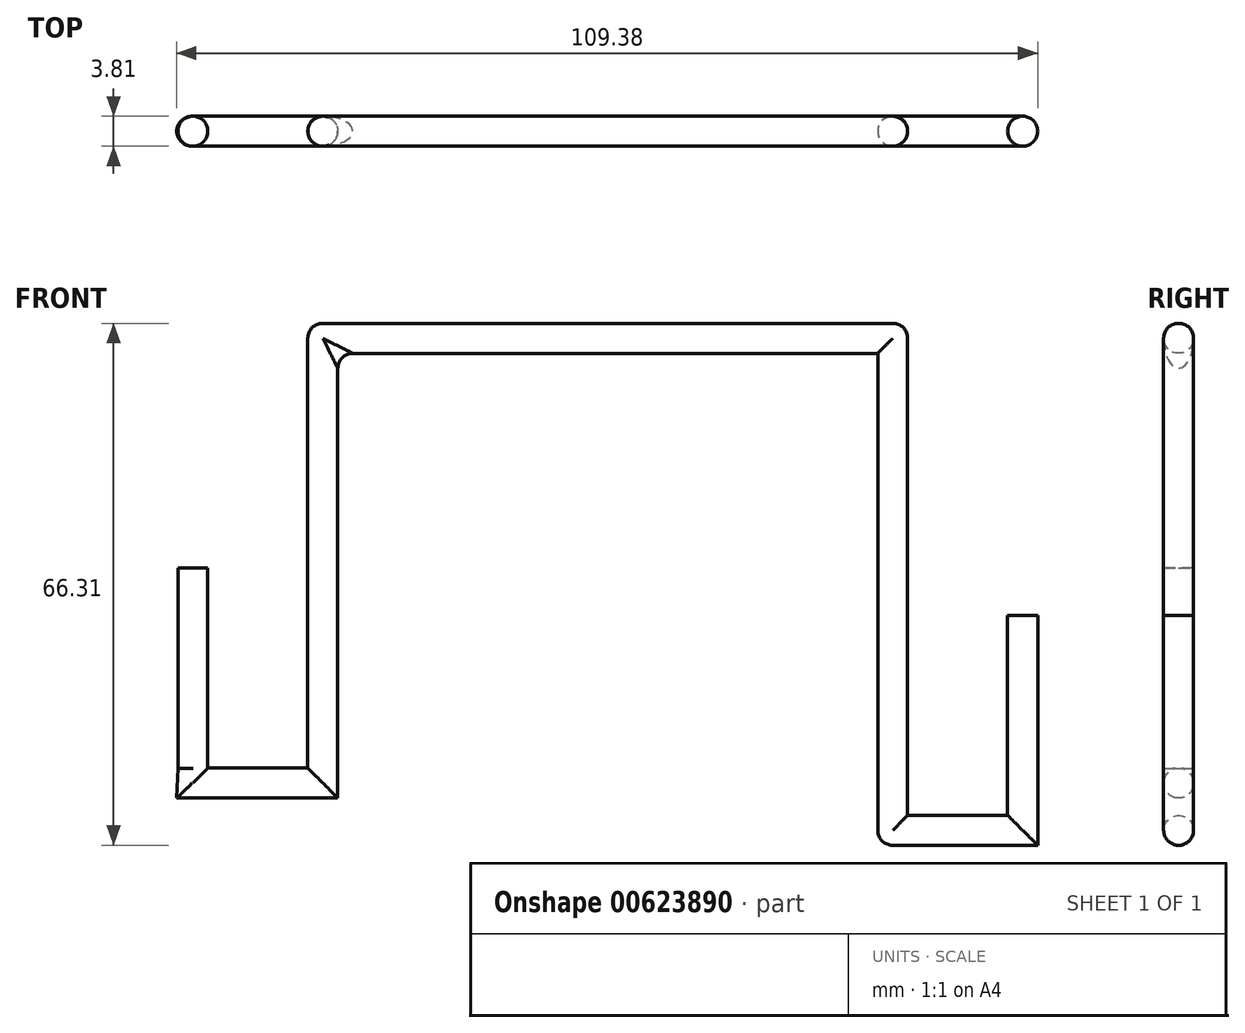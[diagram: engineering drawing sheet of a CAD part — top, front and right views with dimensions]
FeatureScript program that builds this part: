
annotation { "Feature Type Name" : "Feature", "Feature Type Description" : "" }
export const myFeature = defineFeature(function(context is Context, id is Id, definition is map)
    precondition{}
    {
        {
            var Q0;
            Q0=qCreatedBy(makeId("Front.planeOp"),FACE);
            var sketch = newSketch(context, id + "F0", { "sketchPlane" : qUnion([Q0])});
            skLineSegment(sketch, "E0", {"start": v(0, 0) * mm, "end": v(38.1, 0) * mm});
            skLineSegment(sketch, "E1", {"start": v(0, 0) * mm, "end": v(-38.1, 0) * mm});
            skLineSegment(sketch, "E2", {"start": v(38.1, 0) * mm, "end": v(38.1, -62.5) * mm});
            skLineSegment(sketch, "E3", {"start": v(-38.1, 0) * mm, "end": v(-38.1, -56.5) * mm});
            skLineSegment(sketch, "E4", {"start": v(-38.1, -56.5) * mm, "end": v(-50.8, -56.5) * mm});
            skLineSegment(sketch, "E5", {"start": v(-50.8, -56.5) * mm, "end": v(-50.8, -31.1) * mm});
            skLineSegment(sketch, "E6", {"start": v(38.1, -62.5) * mm, "end": v(50.8, -62.5) * mm});
            skLineSegment(sketch, "E7", {"start": v(50.8, -62.5) * mm, "end": v(50.8, -37.1) * mm});
            skLineSegment(sketch, "E8.0", {"start": v(0, -3.81) * mm, "end": v(34.3, -3.81) * mm});
            skLineSegment(sketch, "E8.1", {"start": v(0, -3.8) * mm, "end": v(-34.29, -3.81) * mm});
            skLineSegment(sketch, "E9.0", {"start": v(34.3, -3.81) * mm, "end": v(34.3, -62.5) * mm});
            skLineSegment(sketch, "E10.0", {"start": v(54.61, -62.5) * mm, "end": v(54.61, -37.1) * mm});
            skLineSegment(sketch, "E11.0", {"start": v(-34.29, -3.81) * mm, "end": v(-34.29, -56.5) * mm});
            skLineSegment(sketch, "E12.0", {"start": v(-54.6, -56.5) * mm, "end": v(-54.6, -31.1) * mm});
            skLineSegment(sketch, "E13.0", {"start": v(-38.1, -60.32) * mm, "end": v(-50.96, -60.32) * mm});
            skLineSegment(sketch, "E14.0", {"start": v(38.1, -66.3) * mm, "end": v(50.8, -66.3) * mm});
            skLineSegment(sketch, "E15", {"start": v(50.8, -66.3) * mm, "end": v(54.6, -66.3) * mm});
            skLineSegment(sketch, "E16", {"start": v(54.61, -62.5) * mm, "end": v(54.6, -66.3) * mm});
            skLineSegment(sketch, "E17", {"start": v(-38.1, -60.32) * mm, "end": v(-34.3, -60.32) * mm});
            skLineSegment(sketch, "E18", {"start": v(-50.96, -60.32) * mm, "end": v(-54.77, -60.32) * mm});
            skLineSegment(sketch, "E19", {"start": v(38.1, -66.3) * mm, "end": v(34.29, -66.3) * mm});
            skLineSegment(sketch, "E20", {"start": v(-54.77, -60.32) * mm, "end": v(-54.6, -56.5) * mm});
            skLineSegment(sketch, "E21", {"start": v(-34.3, -60.32) * mm, "end": v(-34.29, -56.5) * mm});
            skLineSegment(sketch, "E22", {"start": v(-54.6, -31.1) * mm, "end": v(-50.8, -31.1) * mm});
            skLineSegment(sketch, "E23", {"start": v(34.29, -66.3) * mm, "end": v(34.3, -62.5) * mm});
            skLineSegment(sketch, "E24", {"start": v(54.61, -37.1) * mm, "end": v(50.8, -37.1) * mm});
            skSolve(sketch);
        }
        {
            var Q0;
            Q0=makeQuery(id+"F0.imprint","IMPRINT",FACE,{"disambiguationData":[TD([[makeQuery(id+"F0.imprint","IMPRINT",EDGE,{"derivedFrom":sQuery(id+"F0.wireOp",EDGE,"E0")}),-1.0]])]});
            extrude(context, id + "F1", {"entities" : qUnion([Q0]), "oppositeDirection" : true, "depth" : 3.8 * mm, "offsetDistance" : 25.4 * mm});
        }
        {
            var Q0;
            Q0=makeQuery(id+"F1.opExtrude","CAP_EDGE",EDGE,{"disambiguationData":[OSD([sQuery(id+"F0.wireOp",EDGE,"E2")])],"isStart":true});
            var Q1;
            Q1=makeQuery(id+"F1.opExtrude","CAP_EDGE",EDGE,{"disambiguationData":[OSD([sQuery(id+"F0.wireOp",EDGE,"E2")])],"isStart":false});
            var Q2;
            Q2=makeQuery(id+"F1.opExtrude","CAP_EDGE",EDGE,{"disambiguationData":[OSD([sQuery(id+"F0.wireOp",EDGE,"E9.0"),sQuery(id+"F0.wireOp",EDGE,"E23")])],"isStart":true});
            var Q3;
            Q3=makeQuery(id+"F1.opExtrude","CAP_EDGE",EDGE,{"disambiguationData":[OSD([sQuery(id+"F0.wireOp",EDGE,"E9.0"),sQuery(id+"F0.wireOp",EDGE,"E23")])],"isStart":false});
            fillet(context, id + "F2", {"entities" : qUnion([Q0, Q1, Q2, Q3]), "radius" : 1.9 * mm, "tangentPropagation" : true, "allowEdgeOverflow" : false});
        }
        {
            var Q0;
            Q0=makeQuery(id+"F1.opExtrude","CAP_EDGE",EDGE,{"disambiguationData":[OSD([sQuery(id+"F0.wireOp",EDGE,"E10.0"),sQuery(id+"F0.wireOp",EDGE,"E16")])],"isStart":false});
            var Q1;
            Q1=makeQuery(id+"F1.opExtrude","CAP_EDGE",EDGE,{"disambiguationData":[OSD([sQuery(id+"F0.wireOp",EDGE,"E7")])],"isStart":false});
            var Q2;
            Q2=makeQuery(id+"F1.opExtrude","CAP_EDGE",EDGE,{"disambiguationData":[OSD([sQuery(id+"F0.wireOp",EDGE,"E10.0"),sQuery(id+"F0.wireOp",EDGE,"E16")])],"isStart":true});
            var Q3;
            Q3=makeQuery(id+"F1.opExtrude","CAP_EDGE",EDGE,{"disambiguationData":[OSD([sQuery(id+"F0.wireOp",EDGE,"E6")])],"isStart":false});
            var Q4;
            Q4=makeQuery(id+"F1.opExtrude","CAP_EDGE",EDGE,{"disambiguationData":[OSD([sQuery(id+"F0.wireOp",EDGE,"E6")])],"isStart":true});
            var Q5;
            Q5=makeQuery(id+"F1.opExtrude","CAP_EDGE",EDGE,{"disambiguationData":[OSD([sQuery(id+"F0.wireOp",EDGE,"E14.0"),sQuery(id+"F0.wireOp",EDGE,"E15"),sQuery(id+"F0.wireOp",EDGE,"E19")])],"isStart":false});
            var Q6;
            Q6=makeQuery(id+"F1.opExtrude","CAP_EDGE",EDGE,{"disambiguationData":[OSD([sQuery(id+"F0.wireOp",EDGE,"E7")])],"isStart":true});
            fillet(context, id + "F3", {"entities" : qUnion([Q0, Q1, Q2, Q3, Q4, Q5, Q6]), "radius" : 1.9 * mm, "tangentPropagation" : true, "allowEdgeOverflow" : false});
        }
        {
            var Q0;
            Q0=makeQuery(id+"F1.opExtrude","CAP_EDGE",EDGE,{"disambiguationData":[OSD([sQuery(id+"F0.wireOp",EDGE,"E0"),sQuery(id+"F0.wireOp",EDGE,"E1")])],"isStart":true});
            var Q1;
            Q1=makeQuery(id+"F1.opExtrude","CAP_EDGE",EDGE,{"disambiguationData":[OSD([sQuery(id+"F0.wireOp",EDGE,"E0"),sQuery(id+"F0.wireOp",EDGE,"E1")])],"isStart":false});
            var Q2;
            Q2=makeQuery(id+"F1.opExtrude","CAP_EDGE",EDGE,{"disambiguationData":[OSD([sQuery(id+"F0.wireOp",EDGE,"E8.0"),sQuery(id+"F0.wireOp",EDGE,"E8.1")])],"isStart":true});
            var Q3;
            Q3=makeQuery(id+"F1.opExtrude","CAP_EDGE",EDGE,{"disambiguationData":[OSD([sQuery(id+"F0.wireOp",EDGE,"E8.0"),sQuery(id+"F0.wireOp",EDGE,"E8.1")])],"isStart":false});
            var Q4;
            Q4=makeQuery(id+"F1.opExtrude","CAP_EDGE",EDGE,{"disambiguationData":[OSD([sQuery(id+"F0.wireOp",EDGE,"E11.0"),sQuery(id+"F0.wireOp",EDGE,"E21")])],"isStart":false});
            var Q5;
            Q5=makeQuery(id+"F1.opExtrude","CAP_EDGE",EDGE,{"disambiguationData":[OSD([sQuery(id+"F0.wireOp",EDGE,"E3")])],"isStart":false});
            var Q6;
            Q6=makeQuery(id+"F1.opExtrude","CAP_EDGE",EDGE,{"disambiguationData":[OSD([sQuery(id+"F0.wireOp",EDGE,"E11.0"),sQuery(id+"F0.wireOp",EDGE,"E21")])],"isStart":true});
            var Q7;
            Q7=makeQuery(id+"F1.opExtrude","CAP_EDGE",EDGE,{"disambiguationData":[OSD([sQuery(id+"F0.wireOp",EDGE,"E12.0")])],"isStart":false});
            var Q8;
            Q8=makeQuery(id+"F1.opExtrude","CAP_EDGE",EDGE,{"disambiguationData":[OSD([sQuery(id+"F0.wireOp",EDGE,"E5")])],"isStart":false});
            var Q9;
            Q9=makeQuery(id+"F1.opExtrude","CAP_EDGE",EDGE,{"disambiguationData":[OSD([sQuery(id+"F0.wireOp",EDGE,"E5")])],"isStart":true});
            var Q10;
            Q10=makeQuery(id+"F1.opExtrude","CAP_EDGE",EDGE,{"disambiguationData":[OSD([sQuery(id+"F0.wireOp",EDGE,"E4")])],"isStart":false});
            var Q11;
            Q11=makeQuery(id+"F1.opExtrude","CAP_EDGE",EDGE,{"disambiguationData":[OSD([sQuery(id+"F0.wireOp",EDGE,"E4")])],"isStart":true});
            var Q12;
            Q12=makeQuery(id+"F1.opExtrude","CAP_EDGE",EDGE,{"disambiguationData":[OSD([sQuery(id+"F0.wireOp",EDGE,"E13.0"),sQuery(id+"F0.wireOp",EDGE,"E17"),sQuery(id+"F0.wireOp",EDGE,"E18")])],"isStart":false});
            var Q13;
            Q13=makeQuery(id+"F1.opExtrude","CAP_EDGE",EDGE,{"disambiguationData":[OSD([sQuery(id+"F0.wireOp",EDGE,"E3")])],"isStart":true});
            var Q14;
            Q14=makeQuery(id+"F1.opExtrude","CAP_EDGE",EDGE,{"disambiguationData":[OSD([sQuery(id+"F0.wireOp",EDGE,"E13.0"),sQuery(id+"F0.wireOp",EDGE,"E17"),sQuery(id+"F0.wireOp",EDGE,"E18")])],"isStart":true});
            var Q15;
            Q15=makeQuery(id+"F1.opExtrude","CAP_EDGE",EDGE,{"disambiguationData":[OSD([sQuery(id+"F0.wireOp",EDGE,"E12.0")])],"isStart":true});
            fillet(context, id + "F4", {"entities" : qUnion([Q0, Q1, Q2, Q3, Q4, Q5, Q6, Q7, Q8, Q9, Q10, Q11, Q12, Q13, Q14, Q15]), "radius" : 1.9 * mm, "tangentPropagation" : true, "allowEdgeOverflow" : false});
        }
        {
            var Q0;
            Q0=makeQuery(id+"F4.opFillet","BLEND_EDGE",EDGE,{"blendedFrom":[makeQuery(id+"F1.opExtrude","CAP_EDGE",EDGE,{"disambiguationData":[OSD([sQuery(id+"F0.wireOp",EDGE,"E3")])],"isStart":true}),makeQuery(id+"F1.opExtrude","CAP_EDGE",EDGE,{"disambiguationData":[OSD([sQuery(id+"F0.wireOp",EDGE,"E0"),sQuery(id+"F0.wireOp",EDGE,"E1")])],"isStart":true})],"blendedInto":[]});
            fillet(context, id + "F5", {"entities" : qUnion([Q0]), "radius" : 1.9 * mm, "tangentPropagation" : true, "allowEdgeOverflow" : false});
        }
    });
